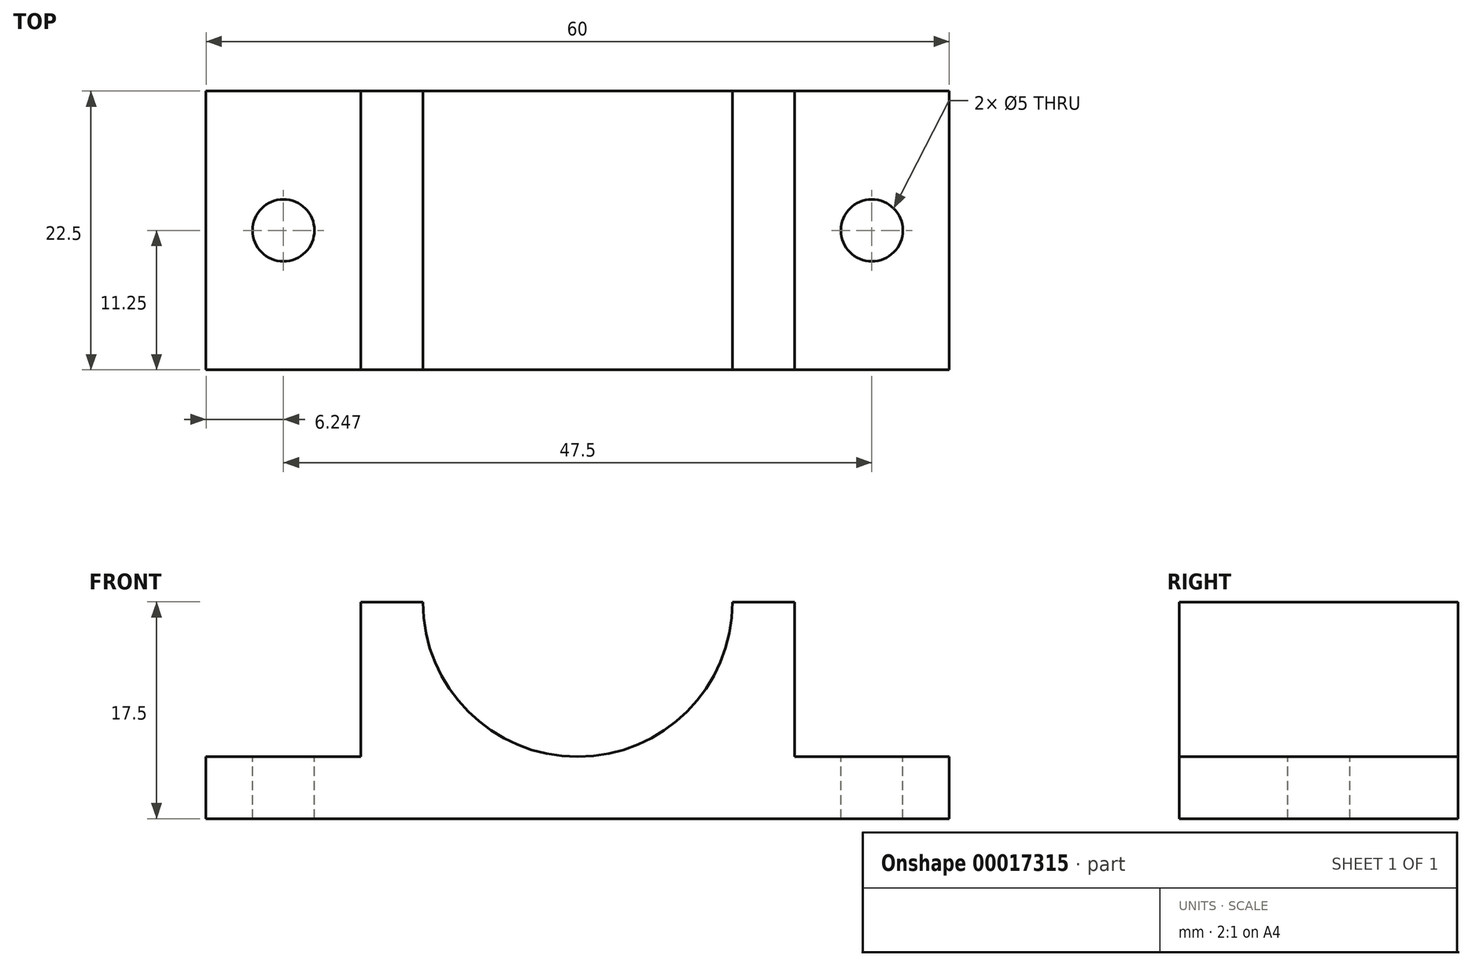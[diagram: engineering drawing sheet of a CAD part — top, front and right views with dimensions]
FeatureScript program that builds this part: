
annotation { "Feature Type Name" : "Feature", "Feature Type Description" : "" }
export const myFeature = defineFeature(function(context is Context, id is Id, definition is map)
    precondition{}
    {
        {
            var Q0;
            Q0=qCreatedBy(makeId("Front.planeOp"),FACE);
            var sketch = newSketch(context, id + "F0", { "sketchPlane" : qUnion([Q0])});
            skLineSegment(sketch, "E0", {"start": v(-48.7, 6.38) * mm, "end": v(-36.2, 6.38) * mm});
            skLineSegment(sketch, "E1", {"start": v(-48.7, 6.38) * mm, "end": v(-48.7, 1.38) * mm});
            skLineSegment(sketch, "E2", {"start": v(-48.7, 1.38) * mm, "end": v(11.3, 1.38) * mm});
            skLineSegment(sketch, "E3", {"start": v(11.3, 1.38) * mm, "end": v(11.3, 6.38) * mm});
            skLineSegment(sketch, "E4", {"start": v(11.3, 6.38) * mm, "end": v(-1.2, 6.38) * mm});
            skLineSegment(sketch, "E5", {"start": v(-1.2, 6.38) * mm, "end": v(-1.2, 18.88) * mm});
            skLineSegment(sketch, "E6", {"start": v(-36.2, 18.88) * mm, "end": v(-36.2, 6.38) * mm});
            skLineSegment(sketch, "E7", {"start": v(-36.2, 18.88) * mm, "end": v(-31.2, 18.88) * mm});
            skLineSegment(sketch, "E8", {"start": v(-1.2, 18.88) * mm, "end": v(-6.2, 18.88) * mm});
            skArc(sketch, "E9", {"start": v(-31.2, 18.88) * mm, "mid": v(-18.7, 6.38) * mm, "end": v(-6.2, 18.88) * mm});
            skSolve(sketch);
        }
        {
            var Q0;
            Q0=makeQuery(id+"F0.imprint","IMPRINT",FACE,{"disambiguationData":[TD([[makeQuery(id+"F0.imprint","IMPRINT",EDGE,{"derivedFrom":sQuery(id+"F0.wireOp",EDGE,"E0")}),-1.0]])]});
            extrude(context, id + "F1", {"entities" : qUnion([Q0]), "depth" : 22.5 * mm});
        }
        {
            var Q0;
            Q0=makeQuery(id+"F1.opExtrude","SWEPT_FACE",FACE,{"disambiguationData":[OSD([sQuery(id+"F0.wireOp",EDGE,"E4")])]});
            var sketch = newSketch(context, id + "F2", { "sketchPlane" : qUnion([Q0])});
            skCircle(sketch, "E10", {"center": v(5.06, -11.25) * mm, "radius": 2.5 * mm});
            skCircle(sketch, "E11", {"center": v(-42.44, -11.25) * mm, "radius": 2.5 * mm});
            skSolve(sketch);
        }
        {
            var Q0;
            Q0=makeQuery(id+"F2.imprint","IMPRINT",FACE,{"disambiguationData":[TD([[makeQuery(id+"F2.imprint","IMPRINT",EDGE,{"derivedFrom":sQuery(id+"F2.wireOp",EDGE,"E11")}),1.0]])]});
            var Q1;
            Q1=makeQuery(id+"F2.imprint","IMPRINT",FACE,{"disambiguationData":[TD([[makeQuery(id+"F2.imprint","IMPRINT",EDGE,{"derivedFrom":sQuery(id+"F2.wireOp",EDGE,"E10")}),1.0]])]});
            extrude(context, id + "F3", {"entities" : qUnion([Q0, Q1]), "operationType" : NewBodyOperationType.REMOVE, "oppositeDirection" : true, "depth" : 5 * mm});
        }
    });
